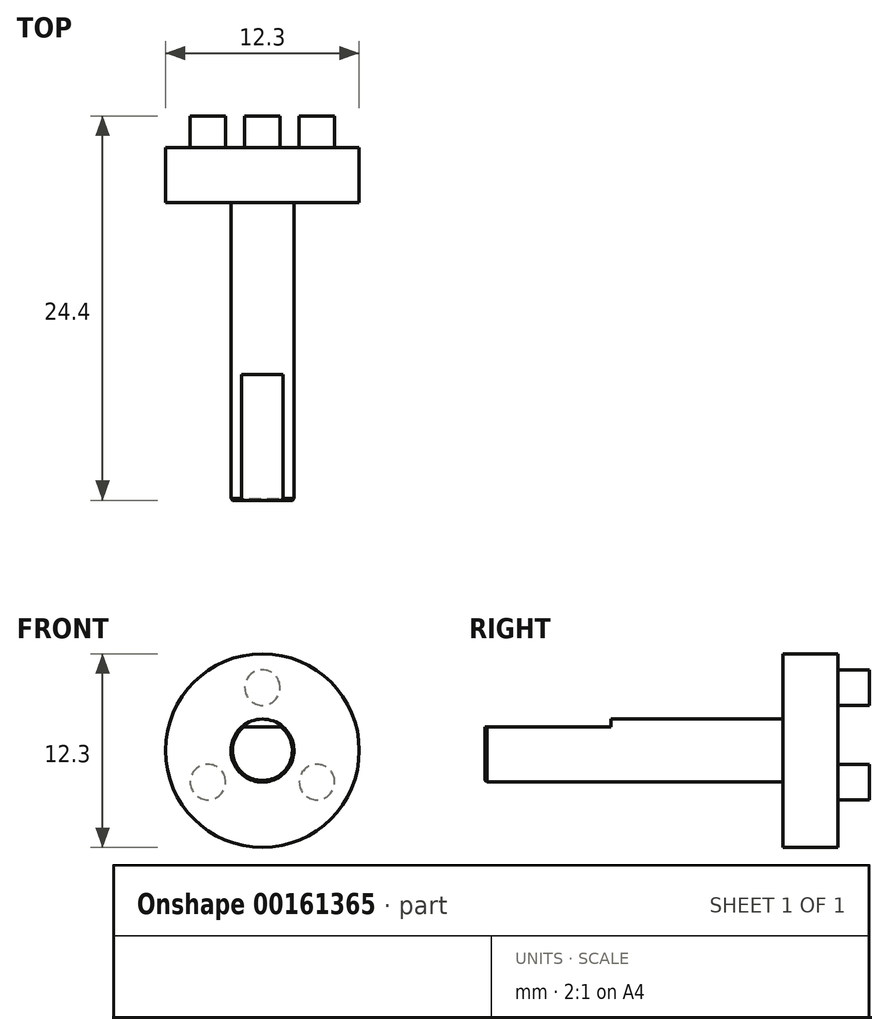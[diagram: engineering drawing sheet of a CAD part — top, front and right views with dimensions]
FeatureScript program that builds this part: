
annotation { "Feature Type Name" : "Feature", "Feature Type Description" : "" }
export const myFeature = defineFeature(function(context is Context, id is Id, definition is map)
    precondition{}
    {
        {
            var Q0;
            Q0=qCreatedBy(makeId("Front.planeOp"),FACE);
            var sketch = newSketch(context, id + "F0", { "sketchPlane" : qUnion([Q0])});
            skCircle(sketch, "E0", {"center": v(0, 0) * mm, "radius": 2 * mm});
            skSolve(sketch);
        }
        {
            var Q0;
            Q0=qSketchRegion(id+"F0",true);
            extrude(context, id + "F1", {"entities" : qUnion([Q0]), "depth" : 18.9 * mm});
        }
        {
            var Q0;
            Q0=makeQuery(id+"F1.opExtrude","CAP_FACE",FACE,{"disambiguationData":[OSD([sQuery(id+"F0.wireOp",EDGE,"E0")])],"isStart":false});
            var sketch = newSketch(context, id + "F2", { "sketchPlane" : qUnion([Q0])});
            skLineSegment(sketch, "E1", {"start": v(-1.32, 1.5) * mm, "end": v(1.32, 1.5) * mm});
            skArc(sketch, "E2", {"start": v(-1.32, 1.5) * mm, "mid": v(0, 2) * mm, "end": v(1.32, 1.5) * mm});
            skSolve(sketch);
        }
        {
            var Q0;
            Q0=qSketchRegion(id+"F2",true);
            extrude(context, id + "F3", {"entities" : qUnion([Q0]), "operationType" : NewBodyOperationType.REMOVE, "oppositeDirection" : true, "depth" : 8 * mm});
        }
        {
            var Q0;
            Q0=makeQuery(id+"F1.opExtrude","CAP_EDGE",EDGE,{"disambiguationData":[OSD([sQuery(id+"F0.wireOp",EDGE,"E0")])],"isStart":false});
            var Q1;
            {var subQ0=sQuery(id+"F2.wireOp",EDGE,"E2");var subQ1=sQuery(id+"F2.wireOp",EDGE,"E1");var subQ2=sQuery(id+"F0.wireOp",EDGE,"E0");Q1=makeQuery(id+"F3.boolean.opBoolean","COPY",EDGE,{"derivedFrom":makeQuery(id+"F3.opExtrude","SWEPT_EDGE",EDGE,{"disambiguationData":[OSD([subQ2,subQ1,subQ0]),TDD([makeQuery(id+"F2.imprint","INTERSECT",VERTEX,{"disambiguationData":[OD(1.0)],"derivedFrom":[makeQuery(id+"F1.opExtrude","CAP_EDGE",EDGE,{"disambiguationData":[OSD([subQ2])],"isStart":false}),subQ1,subQ0]})])]})});}
            var Q2;
            {var subQ0=sQuery(id+"F2.wireOp",EDGE,"E2");var subQ1=sQuery(id+"F2.wireOp",EDGE,"E1");var subQ2=sQuery(id+"F0.wireOp",EDGE,"E0");Q2=makeQuery(id+"F3.boolean.opBoolean","COPY",EDGE,{"derivedFrom":makeQuery(id+"F3.opExtrude","SWEPT_EDGE",EDGE,{"disambiguationData":[OSD([subQ2,subQ1,subQ0]),TDD([makeQuery(id+"F2.imprint","INTERSECT",VERTEX,{"disambiguationData":[OD(0.0)],"derivedFrom":[makeQuery(id+"F1.opExtrude","CAP_EDGE",EDGE,{"disambiguationData":[OSD([subQ2])],"isStart":false}),subQ1,subQ0]})])]})});}
            var Q3;
            Q3=makeQuery(id+"F3.boolean.opBoolean","COPY",EDGE,{"derivedFrom":makeQuery(id+"F3.opExtrude","CAP_EDGE",EDGE,{"disambiguationData":[OSD([sQuery(id+"F2.wireOp",EDGE,"E2")])],"isStart":false})});
            chamfer(context, id + "F4", {"entities" : qUnion([Q0, Q1, Q2, Q3]), "width" : 0.1 * mm, "tangentPropagation" : true});
        }
        {
            var Q0;
            Q0=makeQuery(id+"F1.opExtrude","CAP_FACE",FACE,{"disambiguationData":[OSD([sQuery(id+"F0.wireOp",EDGE,"E0")])],"isStart":true});
            var sketch = newSketch(context, id + "F5", { "sketchPlane" : qUnion([Q0])});
            skCircle(sketch, "E3", {"center": v(0, 0) * mm, "radius": 6.15 * mm});
            skSolve(sketch);
        }
        {
            var Q0;
            Q0=qSketchRegion(id+"F5",true);
            extrude(context, id + "F6", {"entities" : qUnion([Q0]), "operationType" : NewBodyOperationType.ADD, "depth" : 3.5 * mm});
        }
        {
            var Q0;
            Q0=makeQuery(id+"F6.opExtrude","CAP_FACE",FACE,{"disambiguationData":[OSD([sQuery(id+"F5.wireOp",EDGE,"E3")])],"isStart":false});
            var sketch = newSketch(context, id + "F7", { "sketchPlane" : qUnion([Q0])});
            skCircle(sketch, "E4", {"center": v(0, 0) * mm, "radius": 4 * mm, "construction": true});
            skLineSegment(sketch, "E5", {"start": v(0, 0) * mm, "end": v(0, 6.15) * mm, "construction": true});
            skCircle(sketch, "E6", {"center": v(0, 4) * mm, "radius": 1.13 * mm});
            skCircle(sketch, "E7.1.0", {"center": v(-3.46, -2) * mm, "radius": 1.13 * mm});
            skCircle(sketch, "E7.2.0", {"center": v(3.46, -2) * mm, "radius": 1.13 * mm});
            skSolve(sketch);
        }
        {
            var Q0;
            Q0=qSketchRegion(id+"F7",true);
            extrude(context, id + "F8", {"entities" : qUnion([Q0]), "operationType" : NewBodyOperationType.ADD, "depth" : 2 * mm});
        }
    });
